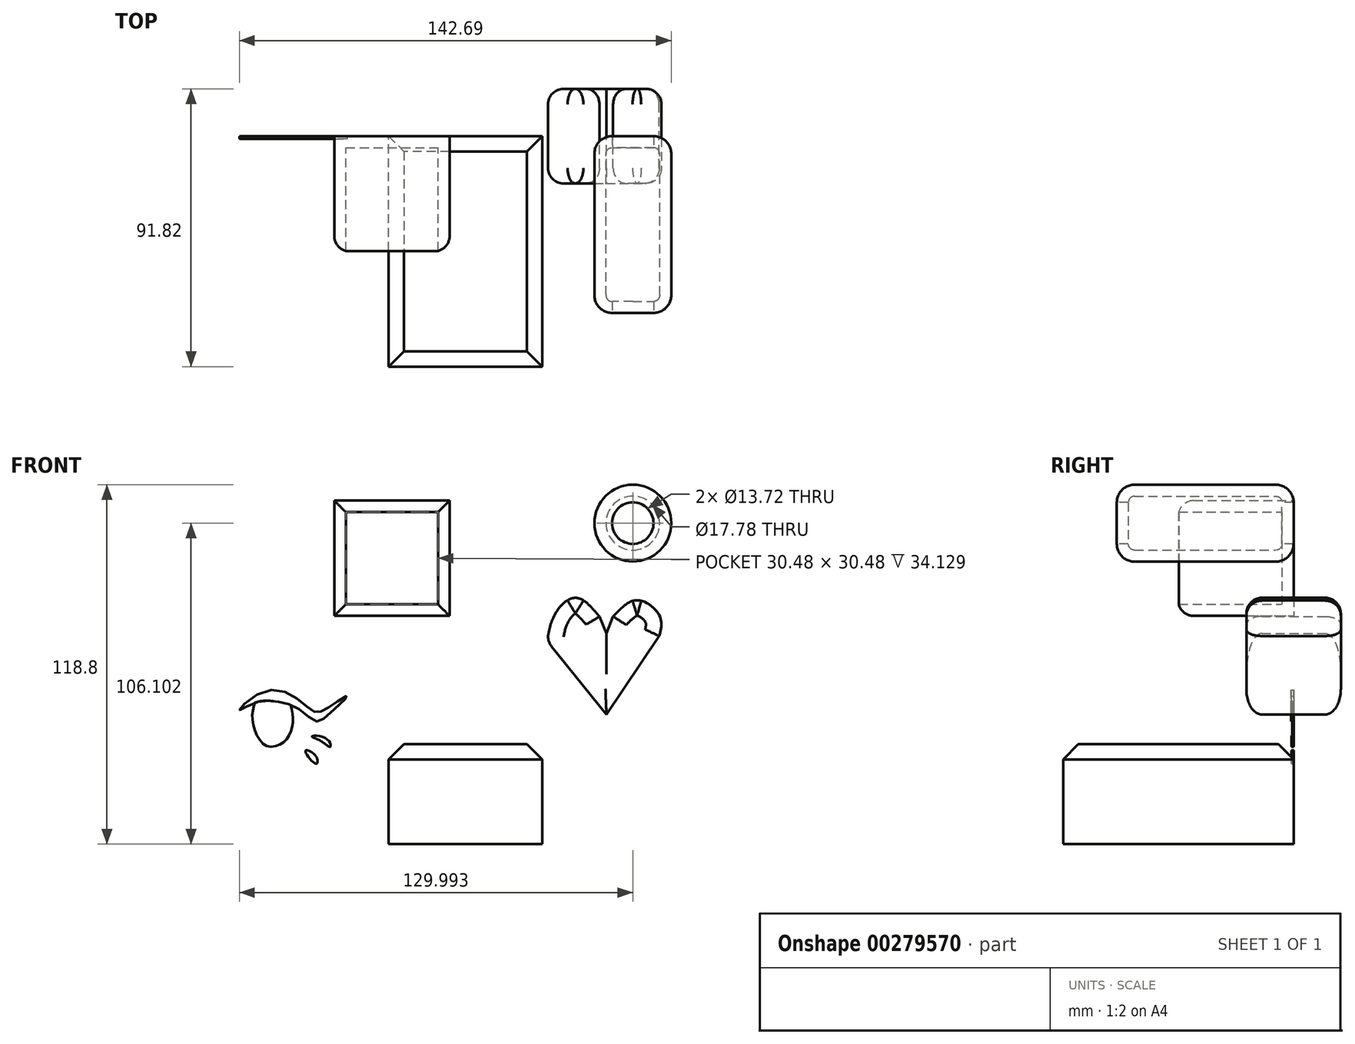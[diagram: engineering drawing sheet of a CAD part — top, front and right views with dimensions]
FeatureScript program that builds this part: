
annotation { "Feature Type Name" : "Feature", "Feature Type Description" : "" }
export const myFeature = defineFeature(function(context is Context, id is Id, definition is map)
    precondition{}
    {
        {
            var Q0;
            Q0=qCreatedBy(makeId("Front.planeOp"),FACE);
            var sketch = newSketch(context, id + "F0", { "sketchPlane" : qUnion([Q0])});
            skLineSegment(sketch, "E0.bottom", {"start": v(-51.88, 58.75) * mm, "end": v(-13.78, 58.75) * mm});
            skLineSegment(sketch, "E0.top", {"start": v(-51.88, 20.65) * mm, "end": v(-13.78, 20.65) * mm});
            skLineSegment(sketch, "E0.left", {"start": v(-51.88, 58.75) * mm, "end": v(-51.88, 20.65) * mm});
            skLineSegment(sketch, "E0.right", {"start": v(-13.78, 58.75) * mm, "end": v(-13.78, 20.65) * mm});
            skSolve(sketch);
        }
        {
            var Q0;
            Q0=qCreatedBy(makeId("Front.planeOp"),FACE);
            var sketch = newSketch(context, id + "F1", { "sketchPlane" : qUnion([Q0])});
            skCircle(sketch, "E1", {"center": v(46.78, 51.3) * mm, "radius": 12.7 * mm});
            skSolve(sketch);
        }
        {
            var Q0;
            Q0=qCreatedBy(makeId("Front.planeOp"),FACE);
            var sketch = newSketch(context, id + "F2", { "sketchPlane" : qUnion([Q0])});
            skLineSegment(sketch, "E2.bottom", {"start": v(-33.9, -21.78) * mm, "end": v(16.9, -21.78) * mm});
            skLineSegment(sketch, "E2.top", {"start": v(-33.9, -54.8) * mm, "end": v(16.9, -54.8) * mm});
            skLineSegment(sketch, "E2.left", {"start": v(-33.9, -21.78) * mm, "end": v(-33.9, -54.8) * mm});
            skLineSegment(sketch, "E2.right", {"start": v(16.9, -21.78) * mm, "end": v(16.9, -54.8) * mm});
            skSolve(sketch);
        }
        {
            var Q0;
            Q0=makeQuery(id+"F0.imprint","IMPRINT",FACE,{"disambiguationData":[TD([[makeQuery(id+"F0.imprint","IMPRINT",EDGE,{"derivedFrom":sQuery(id+"F0.wireOp",EDGE,"E0.bottom")}),-1.0]])]});
            extrude(context, id + "F3", {"entities" : qUnion([Q0]), "depth" : 38.1 * mm});
        }
        {
            var Q0;
            Q0=makeQuery(id+"F1.imprint","IMPRINT",FACE,{"disambiguationData":[TD([[makeQuery(id+"F1.imprint","IMPRINT",EDGE,{"derivedFrom":sQuery(id+"F1.wireOp",EDGE,"E1")}),1.0]])]});
            extrude(context, id + "F4", {"entities" : qUnion([Q0]), "depth" : 58.42 * mm});
        }
        {
            var Q0;
            Q0=makeQuery(id+"F2.imprint","IMPRINT",FACE,{"disambiguationData":[TD([[makeQuery(id+"F2.imprint","IMPRINT",EDGE,{"derivedFrom":sQuery(id+"F2.wireOp",EDGE,"E2.bottom")}),-1.0]])]});
            extrude(context, id + "F5", {"entities" : qUnion([Q0]), "depth" : 76.2 * mm});
        }
        {
            var Q0;
            Q0=makeQuery(id+"F4.opExtrude","CAP_EDGE",EDGE,{"disambiguationData":[OSD([sQuery(id+"F1.wireOp",EDGE,"E1")])],"isStart":false});
            var Q1;
            Q1=makeQuery(id+"F4.opExtrude","CAP_EDGE",EDGE,{"disambiguationData":[OSD([sQuery(id+"F1.wireOp",EDGE,"E1")])],"isStart":true});
            fillet(context, id + "F6", {"entities" : qUnion([Q0, Q1]), "radius" : 5.84 * mm, "tangentPropagation" : true, "allowEdgeOverflow" : false});
        }
        {
            var Q0;
            Q0=makeQuery(id+"F3.opExtrude","CAP_FACE",FACE,{"disambiguationData":[OSD([sQuery(id+"F0.wireOp",EDGE,"E0.bottom"),sQuery(id+"F0.wireOp",EDGE,"E0.top"),sQuery(id+"F0.wireOp",EDGE,"E0.left"),sQuery(id+"F0.wireOp",EDGE,"E0.right")])],"isStart":false});
            var Q1;
            Q1=makeQuery(id+"F4.opExtrude","CAP_FACE",FACE,{"disambiguationData":[OSD([sQuery(id+"F1.wireOp",EDGE,"E1")])],"isStart":false});
            var Q2;
            Q2=makeQuery(id+"F4.opExtrude","CAP_FACE",FACE,{"disambiguationData":[OSD([sQuery(id+"F1.wireOp",EDGE,"E1")])],"isStart":true});
            shell(context, id + "F7", {"entities" : qUnion([Q0, Q1, Q2]), "thickness" : 3.8 * mm});
        }
        {
            var Q0;
            Q0=makeQuery(id+"F3.opExtrude","CAP_EDGE",EDGE,{"disambiguationData":[OSD([sQuery(id+"F0.wireOp",EDGE,"E0.right")])],"isStart":false});
            var Q1;
            Q1=makeQuery(id+"F3.opExtrude","CAP_EDGE",EDGE,{"disambiguationData":[OSD([sQuery(id+"F0.wireOp",EDGE,"E0.left")])],"isStart":false});
            var Q2;
            Q2=makeQuery(id+"F3.opExtrude","CAP_EDGE",EDGE,{"disambiguationData":[OSD([sQuery(id+"F0.wireOp",EDGE,"E0.top")])],"isStart":false});
            var Q3;
            Q3=makeQuery(id+"F3.opExtrude","CAP_EDGE",EDGE,{"disambiguationData":[OSD([sQuery(id+"F0.wireOp",EDGE,"E0.bottom")])],"isStart":false});
            fillet(context, id + "F8", {"entities" : qUnion([Q0, Q1, Q2, Q3]), "radius" : 5.08 * mm, "tangentPropagation" : true, "allowEdgeOverflow" : false});
        }
        {
            var Q0;
            Q0=makeQuery(id+"F5.opExtrude","CAP_EDGE",EDGE,{"disambiguationData":[OSD([sQuery(id+"F2.wireOp",EDGE,"E2.bottom")])],"isStart":false});
            var Q1;
            Q1=makeQuery(id+"F5.opExtrude","SWEPT_EDGE",EDGE,{"disambiguationData":[OSD([sQuery(id+"F2.wireOp",EDGE,"E2.bottom"),sQuery(id+"F2.wireOp",EDGE,"E2.right")])]});
            var Q2;
            Q2=makeQuery(id+"F5.opExtrude","SWEPT_EDGE",EDGE,{"disambiguationData":[OSD([sQuery(id+"F2.wireOp",EDGE,"E2.bottom"),sQuery(id+"F2.wireOp",EDGE,"E2.left")])]});
            var Q3;
            Q3=makeQuery(id+"F5.opExtrude","CAP_EDGE",EDGE,{"disambiguationData":[OSD([sQuery(id+"F2.wireOp",EDGE,"E2.bottom")])],"isStart":true});
            chamfer(context, id + "F9", {"entities" : qUnion([Q0, Q1, Q2, Q3]), "width" : 5.08 * mm, "tangentPropagation" : true});
        }
        {
            var Q0;
            Q0=qCreatedBy(makeId("Front.planeOp"),FACE);
            var sketch = newSketch(context, id + "F10", { "sketchPlane" : qUnion([Q0])});
            skLineSegment(sketch, "E3", {"start": v(18.46, 12.36) * mm, "end": v(38.1, -11.94) * mm});
            skLineSegment(sketch, "E4", {"start": v(38.1, -11.94) * mm, "end": v(55.51, 14) * mm});
            skFitSpline(sketch, "E5", {"points": [v(18.46, 12.36) * mm, v(21.32, 21.68) * mm, v(27.92, 26.62) * mm, v(35.75, 20.44) * mm], "startDerivative": vector(5.02, 28.28) * mm, "endDerivative": vector(22.31, -26.5) * mm});
            skLineSegment(sketch, "E6", {"start": v(35.75, 20.44) * mm, "end": v(38.01, 14.88) * mm});
            skLineSegment(sketch, "E7", {"start": v(38.01, 14.88) * mm, "end": v(40.28, 20.44) * mm});
            skFitSpline(sketch, "E8", {"points": [v(40.28, 20.44) * mm, v(43.37, 23.53) * mm, v(48.73, 25.8) * mm, v(55.73, 20.44) * mm, v(55.51, 14) * mm], "startDerivative": vector(13.43, 14.6) * mm, "endDerivative": vector(-6.96, -25.32) * mm});
            skSolve(sketch);
        }
        {
            var Q0;
            Q0=makeQuery(id+"F10.imprint","IMPRINT",FACE,{"disambiguationData":[TD([[makeQuery(id+"F10.imprint","IMPRINT",EDGE,{"derivedFrom":sQuery(id+"F10.wireOp",EDGE,"E3")}),1.0]])]});
            extrude(context, id + "F11", {"entities" : qUnion([Q0]), "endBound" : BoundingType.SYMMETRIC, "depth" : 31.24 * mm});
        }
        {
            var Q0;
            Q0=makeQuery(id+"F11.opExtrude","CAP_FACE",FACE,{"disambiguationData":[OSD([sQuery(id+"F10.wireOp",EDGE,"E3"),sQuery(id+"F10.wireOp",EDGE,"E4"),sQuery(id+"F10.wireOp",EDGE,"E5"),sQuery(id+"F10.wireOp",EDGE,"E6"),sQuery(id+"F10.wireOp",EDGE,"E7"),sQuery(id+"F10.wireOp",EDGE,"E8")])],"isStart":false});
            var Q1;
            Q1=makeQuery(id+"F11.opExtrude","SWEPT_EDGE",EDGE,{"disambiguationData":[OSD([sQuery(id+"F10.wireOp",EDGE,"E3"),sQuery(id+"F10.wireOp",EDGE,"E5")])]});
            var Q2;
            Q2=makeQuery(id+"F11.opExtrude","CAP_FACE",FACE,{"disambiguationData":[OSD([sQuery(id+"F10.wireOp",EDGE,"E3"),sQuery(id+"F10.wireOp",EDGE,"E4"),sQuery(id+"F10.wireOp",EDGE,"E5"),sQuery(id+"F10.wireOp",EDGE,"E6"),sQuery(id+"F10.wireOp",EDGE,"E7"),sQuery(id+"F10.wireOp",EDGE,"E8")])],"isStart":true});
            fillet(context, id + "F12", {"entities" : qUnion([Q0, Q1, Q2]), "radius" : 5.08 * mm, "tangentPropagation" : true, "allowEdgeOverflow" : false});
        }
        {
            var Q0;
            Q0=qCreatedBy(makeId("Front.planeOp"),FACE);
            var sketch = newSketch(context, id + "F13", { "sketchPlane" : qUnion([Q0])});
            skFitSpline(sketch, "E9", {"points": [v(-83.2, -10.37) * mm, v(-76.29, -4.78) * mm, v(-65.4, -5.85) * mm, v(-58.74, -10.9) * mm, v(-56.09, -10.9) * mm, v(-51.3, -7.97) * mm, v(-47.58, -5.85) * mm, v(-54.76, -12.76) * mm, v(-58.21, -14.09) * mm, v(-64.6, -9.57) * mm, v(-70.97, -7.7) * mm, v(-77.88, -7.97) * mm, v(-83.2, -10.37) * mm]});
            skSolve(sketch);
        }
        {
            var Q0;
            Q0=qCreatedBy(makeId("Front.planeOp"),FACE);
            var sketch = newSketch(context, id + "F14", { "sketchPlane" : qUnion([Q0])});
            skFitSpline(sketch, "E10", {"points": [v(-77.88, -7.44) * mm, v(-78.95, -13.82) * mm, v(-74.7, -22.06) * mm, v(-68.58, -21) * mm, v(-65.66, -14.89) * mm, v(-66.45, -7.97) * mm], "startDerivative": vector(-10.28, -30.22) * mm, "endDerivative": vector(-7.72, 34.76) * mm});
            skFitSpline(sketch, "E11", {"points": [v(-77.88, -7.44) * mm, v(-72.83, -5.32) * mm, v(-66.45, -7.97) * mm], "startDerivative": vector(10.4, 6.76) * mm, "endDerivative": vector(12.41, -7.55) * mm});
            skSolve(sketch);
        }
        {
            var Q0;
            Q0=qCreatedBy(makeId("Front.planeOp"),FACE);
            var sketch = newSketch(context, id + "F15", { "sketchPlane" : qUnion([Q0])});
            skFitSpline(sketch, "E12", {"points": [v(-59.28, -19.14) * mm, v(-54.5, -19.94) * mm, v(-53.16, -22.6) * mm, v(-56.35, -20.73) * mm, v(-59.28, -19.14) * mm]});
            skFitSpline(sketch, "E13", {"points": [v(-61.4, -23.92) * mm, v(-57.95, -25.78) * mm, v(-57.95, -28.18) * mm, v(-61.4, -23.92) * mm]});
            skSolve(sketch);
        }
        {
            var Q0;
            Q0=makeQuery(id+"F13.imprint","IMPRINT",FACE,{"disambiguationData":[TD([[makeQuery(id+"F13.imprint","IMPRINT",EDGE,{"derivedFrom":sQuery(id+"F13.wireOp",EDGE,"E9")}),-1.0]])]});
            extrude(context, id + "F16", {"entities" : qUnion([Q0]), "depth" : 0.89 * mm});
        }
        {
            var Q0;
            Q0=makeQuery(id+"F15.imprint","IMPRINT",FACE,{"disambiguationData":[TD([[makeQuery(id+"F15.imprint","IMPRINT",EDGE,{"derivedFrom":sQuery(id+"F15.wireOp",EDGE,"E13")}),-1.0]])]});
            var Q1;
            Q1=makeQuery(id+"F15.imprint","IMPRINT",FACE,{"disambiguationData":[TD([[makeQuery(id+"F15.imprint","IMPRINT",EDGE,{"derivedFrom":sQuery(id+"F15.wireOp",EDGE,"E12")}),-1.0]])]});
            extrude(context, id + "F17", {"entities" : qUnion([Q0, Q1]), "depth" : 0.76 * mm});
        }
        {
            var Q0;
            Q0=makeQuery(id+"F14.imprint","IMPRINT",FACE,{"disambiguationData":[TD([[makeQuery(id+"F14.imprint","IMPRINT",EDGE,{"derivedFrom":sQuery(id+"F14.wireOp",EDGE,"E10")}),1.0]])]});
            extrude(context, id + "F18", {"entities" : qUnion([Q0]), "operationType" : NewBodyOperationType.ADD, "depth" : 0.5 * mm});
        }
    });
